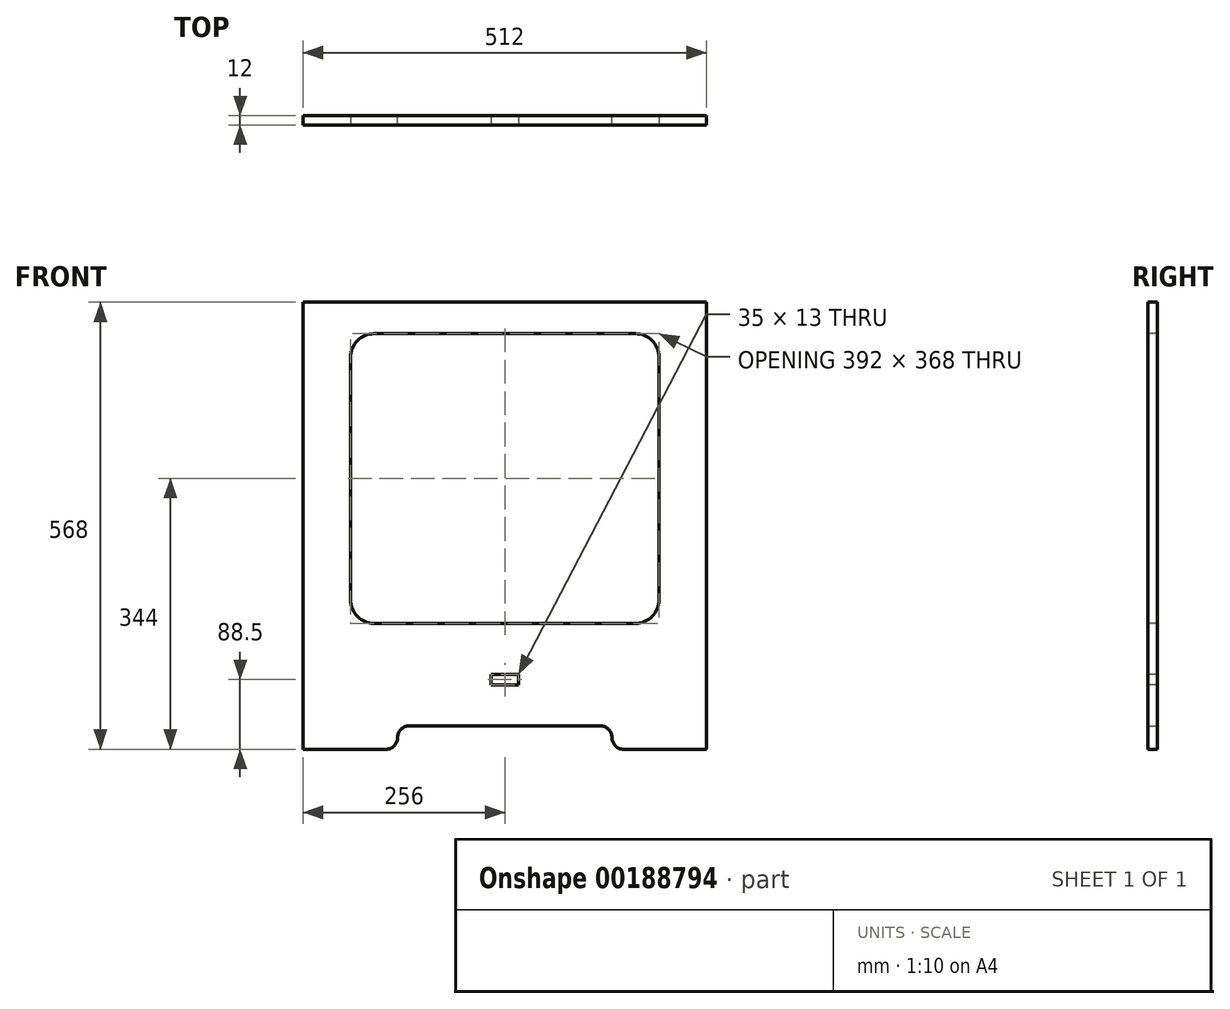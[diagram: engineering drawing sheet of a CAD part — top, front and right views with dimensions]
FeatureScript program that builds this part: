
annotation { "Feature Type Name" : "Feature", "Feature Type Description" : "" }
export const myFeature = defineFeature(function(context is Context, id is Id, definition is map)
    precondition{}
    {
        {
            assignVariable(context, id + "F0", {"name" : "thickness", "anyValue" : 12});
        }
        {
            var Q0;
            Q0=qCreatedBy(makeId("Front.planeOp"),FACE);
            var sketch = newSketch(context, id + "F1", { "sketchPlane" : qUnion([Q0])});
            skLineSegment(sketch, "E0.bottom", {"start": v(256, 284) * mm, "end": v(-256, 284) * mm});
            skLineSegment(sketch, "E0.top", {"start": v(256, -284) * mm, "end": v(-256, -284) * mm});
            skLineSegment(sketch, "E0.left", {"start": v(256, 284) * mm, "end": v(256, -284) * mm});
            skLineSegment(sketch, "E0.right", {"start": v(-256, 284) * mm, "end": v(-256, -284) * mm});
            skPoint(sketch, "E0.middle", {"position": v(0, 0) * mm});
            skLineSegment(sketch, "E1", {"start": v(-136, -254) * mm, "end": v(136, -254) * mm});
            skLineSegment(sketch, "E2", {"start": v(0, 284) * mm, "end": v(0, -284) * mm, "construction": true});
            skLineSegment(sketch, "E3", {"start": v(-136, -254) * mm, "end": v(-136, -284) * mm});
            skLineSegment(sketch, "E4", {"start": v(136, -254) * mm, "end": v(136, -284) * mm});
            skSolve(sketch);
        }
        {
            var Q0;
            Q0=makeQuery(id+"F1.imprint","IMPRINT",FACE,{"disambiguationData":[TD([[makeQuery(id+"F1.imprint","IMPRINT",EDGE,{"derivedFrom":sQuery(id+"F1.wireOp",EDGE,"E0.bottom")}),1.0]])]});
            extrude(context, id + "F2", {"entities" : qUnion([Q0]), "depth" : (getVariable(context, 'thickness')) * mm});
        }
        {
            var Q0;
            Q0=makeQuery(id+"F2.opExtrude","CAP_FACE",FACE,{"disambiguationData":[OSD([sQuery(id+"F1.wireOp",EDGE,"E0.bottom"),sQuery(id+"F1.wireOp",EDGE,"E0.top"),sQuery(id+"F1.wireOp",EDGE,"E0.left"),sQuery(id+"F1.wireOp",EDGE,"E0.right")])],"isStart":false});
            var sketch = newSketch(context, id + "F3", { "sketchPlane" : qUnion([Q0])});
            skLineSegment(sketch, "E5", {"start": v(244, 284) * mm, "end": v(244, -284) * mm, "construction": true});
            skLineSegment(sketch, "E6", {"start": v(-196, -124) * mm, "end": v(-196, 244) * mm});
            skLineSegment(sketch, "E7", {"start": v(-196, 244) * mm, "end": v(196, 244) * mm});
            skLineSegment(sketch, "E8", {"start": v(196, 244) * mm, "end": v(196, -124) * mm});
            skLineSegment(sketch, "E9", {"start": v(196, -124) * mm, "end": v(-196, -124) * mm});
            skLineSegment(sketch, "E10", {"start": v(0, -254) * mm, "end": v(0, 0) * mm, "construction": true});
            skLineSegment(sketch, "E11.bottom", {"start": v(17.5, -189) * mm, "end": v(-17.5, -189) * mm});
            skLineSegment(sketch, "E11.top", {"start": v(17.5, -202) * mm, "end": v(-17.5, -202) * mm});
            skLineSegment(sketch, "E11.left", {"start": v(17.5, -189) * mm, "end": v(17.5, -202) * mm});
            skLineSegment(sketch, "E11.right", {"start": v(-17.5, -189) * mm, "end": v(-17.5, -202) * mm});
            skPoint(sketch, "E11.middle", {"position": v(0, -195.5) * mm});
            skLineSegment(sketch, "E12", {"start": v(-256, -184) * mm, "end": v(256, -184) * mm, "construction": true});
            skSolve(sketch);
        }
        {
            var Q0;
            Q0=makeQuery(id+"F3.imprint","IMPRINT",FACE,{"disambiguationData":[TD([[makeQuery(id+"F3.imprint","IMPRINT",EDGE,{"derivedFrom":sQuery(id+"F3.wireOp",EDGE,"E6")}),-1.0]])]});
            var Q1;
            Q1=makeQuery(id+"F3.imprint","IMPRINT",FACE,{"disambiguationData":[TD([[makeQuery(id+"F3.imprint","IMPRINT",EDGE,{"derivedFrom":sQuery(id+"F3.wireOp",EDGE,"2Nu6wPIc-HMpt-G7lD-CmD9-txG5OiYDfYpH")}),1.0]])]});
            var Q2;
            Q2=makeQuery(id+"F3.imprint","IMPRINT",FACE,{"disambiguationData":[TD([[makeQuery(id+"F3.imprint","IMPRINT",EDGE,{"derivedFrom":sQuery(id+"F3.wireOp",EDGE,"PFvWvd7b-j9xQ-8yW6-2hqE-kbb2U6XiGgEh")}),1.0]])]});
            var Q3;
            Q3=makeQuery(id+"F3.imprint","IMPRINT",FACE,{"disambiguationData":[TD([[makeQuery(id+"F3.imprint","IMPRINT",EDGE,{"derivedFrom":sQuery(id+"F3.wireOp",EDGE,"ohochFCk-nV7A-P8Pk-HXpI-JIOpwZEjfZIJ")}),1.0]])]});
            var Q4;
            Q4=makeQuery(id+"F3.imprint","IMPRINT",FACE,{"disambiguationData":[TD([[makeQuery(id+"F3.imprint","IMPRINT",EDGE,{"derivedFrom":sQuery(id+"F3.wireOp",EDGE,"rfRGOpao-Xdt9-MJzD-lsGe-Q2CHM7OQtzrS")}),1.0]])]});
            var Q5;
            Q5=makeQuery(id+"F3.imprint","IMPRINT",FACE,{"disambiguationData":[TD([[makeQuery(id+"F3.imprint","IMPRINT",EDGE,{"derivedFrom":sQuery(id+"F3.wireOp",EDGE,"48d9157e-a286-4d7f-83ff-f49b96b22439.0.startCap")}),-1.0]])]});
            var Q6;
            Q6=makeQuery(id+"F3.imprint","IMPRINT",FACE,{"disambiguationData":[TD([[makeQuery(id+"F3.imprint","IMPRINT",EDGE,{"derivedFrom":sQuery(id+"F3.wireOp",EDGE,"E11.bottom")}),1.0]])]});
            extrude(context, id + "F4", {"entities" : qUnion([Q0, Q1, Q2, Q3, Q4, Q5, Q6]), "operationType" : NewBodyOperationType.REMOVE, "endBound" : BoundingType.UP_TO_NEXT, "oppositeDirection" : true, "depth" : 25 * mm});
        }
        {
            var Q0;
            Q0=makeQuery(id+"F4.boolean.opBoolean","COPY",EDGE,{"derivedFrom":makeQuery(id+"F4.opExtrude","SWEPT_EDGE",EDGE,{"disambiguationData":[OSD([sQuery(id+"F3.wireOp",EDGE,"E6"),sQuery(id+"F3.wireOp",EDGE,"E9")])]})});
            var Q1;
            Q1=makeQuery(id+"F4.boolean.opBoolean","COPY",EDGE,{"derivedFrom":makeQuery(id+"F4.opExtrude","SWEPT_EDGE",EDGE,{"disambiguationData":[OSD([sQuery(id+"F3.wireOp",EDGE,"E6"),sQuery(id+"F3.wireOp",EDGE,"E7")])]})});
            var Q2;
            Q2=makeQuery(id+"F4.boolean.opBoolean","COPY",EDGE,{"derivedFrom":makeQuery(id+"F4.opExtrude","SWEPT_EDGE",EDGE,{"disambiguationData":[OSD([sQuery(id+"F3.wireOp",EDGE,"E7"),sQuery(id+"F3.wireOp",EDGE,"E8")])]})});
            var Q3;
            Q3=makeQuery(id+"F4.boolean.opBoolean","COPY",EDGE,{"derivedFrom":makeQuery(id+"F4.opExtrude","SWEPT_EDGE",EDGE,{"disambiguationData":[OSD([sQuery(id+"F3.wireOp",EDGE,"E8"),sQuery(id+"F3.wireOp",EDGE,"iu2vll2C-IriT-iNRP-IQoL-HgqayTChKNTE")])]})});
            var Q4;
            Q4=makeQuery(id+"F4.boolean.opBoolean","COPY",EDGE,{"derivedFrom":makeQuery(id+"F4.opExtrude","SWEPT_EDGE",EDGE,{"disambiguationData":[OSD([sQuery(id+"F3.wireOp",EDGE,"zwp6p9vD-zq3E-Q584-GfpK-z8S4uYxaqRPD"),sQuery(id+"F3.wireOp",EDGE,"E9")])]})});
            fillet(context, id + "F5", {"entities" : qUnion([Q0, Q1, Q2, Q3, Q4]), "radius" : 30 * mm, "tangentPropagation" : true, "allowEdgeOverflow" : false});
        }
        {
            var Q0;
            Q0=makeQuery(id+"F2.opExtrude","SWEPT_EDGE",EDGE,{"disambiguationData":[OSD([sQuery(id+"F1.wireOp",EDGE,"E0.top"),sQuery(id+"F1.wireOp",EDGE,"E3")])]});
            var Q1;
            Q1=makeQuery(id+"F2.opExtrude","SWEPT_EDGE",EDGE,{"disambiguationData":[OSD([sQuery(id+"F1.wireOp",EDGE,"E1"),sQuery(id+"F1.wireOp",EDGE,"E3")])]});
            var Q2;
            Q2=makeQuery(id+"F2.opExtrude","SWEPT_EDGE",EDGE,{"disambiguationData":[OSD([sQuery(id+"F1.wireOp",EDGE,"E0.top"),sQuery(id+"F1.wireOp",EDGE,"E4")])]});
            var Q3;
            Q3=makeQuery(id+"F2.opExtrude","SWEPT_EDGE",EDGE,{"disambiguationData":[OSD([sQuery(id+"F1.wireOp",EDGE,"E1"),sQuery(id+"F1.wireOp",EDGE,"E4")])]});
            fillet(context, id + "F6", {"entities" : qUnion([Q0, Q1, Q2, Q3]), "radius" : 15 * mm, "tangentPropagation" : true, "allowEdgeOverflow" : false});
        }
    });
